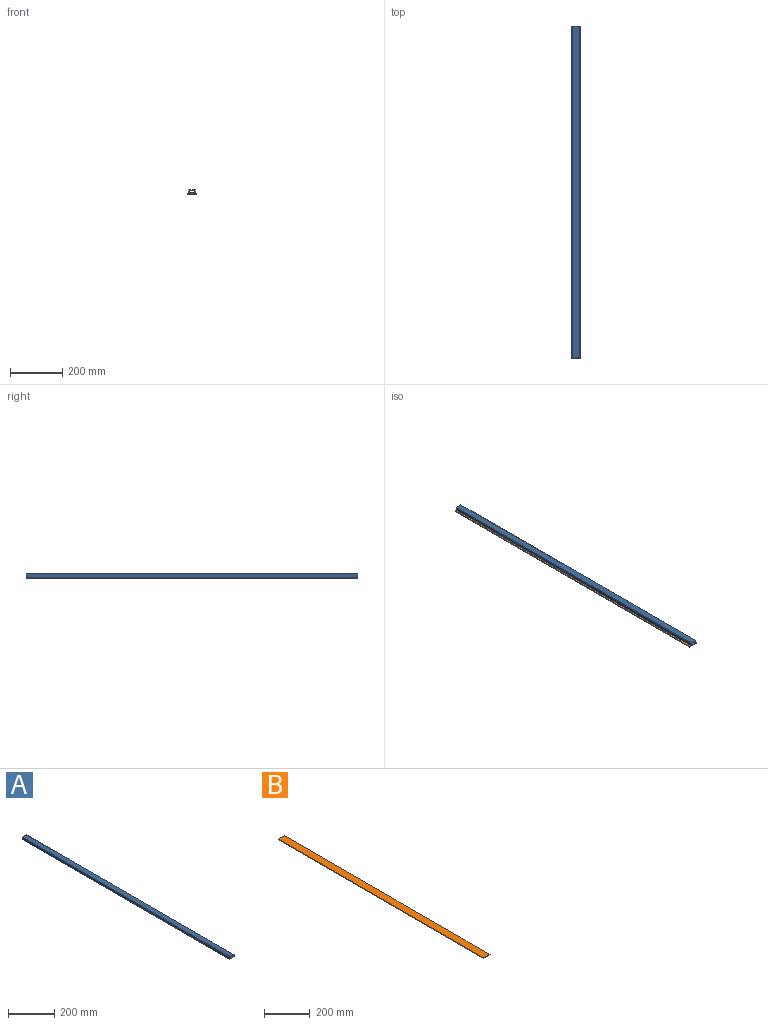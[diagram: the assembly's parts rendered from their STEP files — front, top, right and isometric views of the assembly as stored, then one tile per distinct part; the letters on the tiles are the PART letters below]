
ASSEMBLY  parts=2 mates=1
PART A: 10 faces, bbox 25.4x1270x12.7 mm
  f0: plane 25.4x12.7mm, normal (0,1,0), area 110.9mm2, adj f2,f3,f4,f5,f6,f7,f8,f9
  f1: plane 25.4x12.7mm, normal (0,-1,0), area 110.9mm2, adj f2,f3,f4,f5,f6,f7,f8,f9
  f2: plane 1270x12.7mm, normal (-1,0,0), area 16129mm2, adj f0,f1,f3,f5
  f3: plane 1270x25.4mm, normal (0,0,1), area 32258mm2, adj f0,f1,f2,f4
  f4: plane 1270x12.7mm, normal (1,0,0), area 16129mm2, adj f0,f1,f3,f5
  f5: plane 1270x25.4mm, normal (0,0,-1), area 32258mm2, adj f0,f1,f2,f4
  f6: plane 1270x9.53mm, normal (1,0,0), area 12096.8mm2, adj f0,f1,f7,f9
  f7: plane 1270x22.23mm, normal (0,0,-1), area 28225.7mm2, adj f0,f1,f6,f8
  f8: plane 1270x9.53mm, normal (-1,0,0), area 12096.8mm2, adj f0,f1,f7,f9
  f9: plane 1270x22.23mm, normal (0,0,1), area 28225.8mm2, adj f0,f1,f6,f8
PART B: 6 faces, bbox 38.1x1270x3.2 mm
  f0: plane 38.1x3.18mm, normal (0,1,0), area 121mm2, adj f1,f3,f4,f5
  f1: plane 1270x38.1mm, normal (0,0,1), area 48387mm2, adj f0,f2,f3,f4
  f2: plane 38.1x3.18mm, normal (0,-1,0), area 121mm2, adj f1,f3,f4,f5
  f3: plane 1270x3.18mm, normal (1,0,0), area 4032.3mm2, adj f0,f1,f2,f5
  f4: plane 1270x3.18mm, normal (-1,0,0), area 4032.3mm2, adj f0,f1,f2,f5
  f5: plane 1270x38.1mm, normal (0,0,-1), area 48387mm2, adj f0,f2,f3,f4
PLACE A t=(0,-12.7,-276.23)mm fixed
PLACE B t=(0,-12.7,-285.75)mm
MATE fastened B.f2 <-> A.f1  axis (0,-1,0) through (0,0,-12.7)mm
